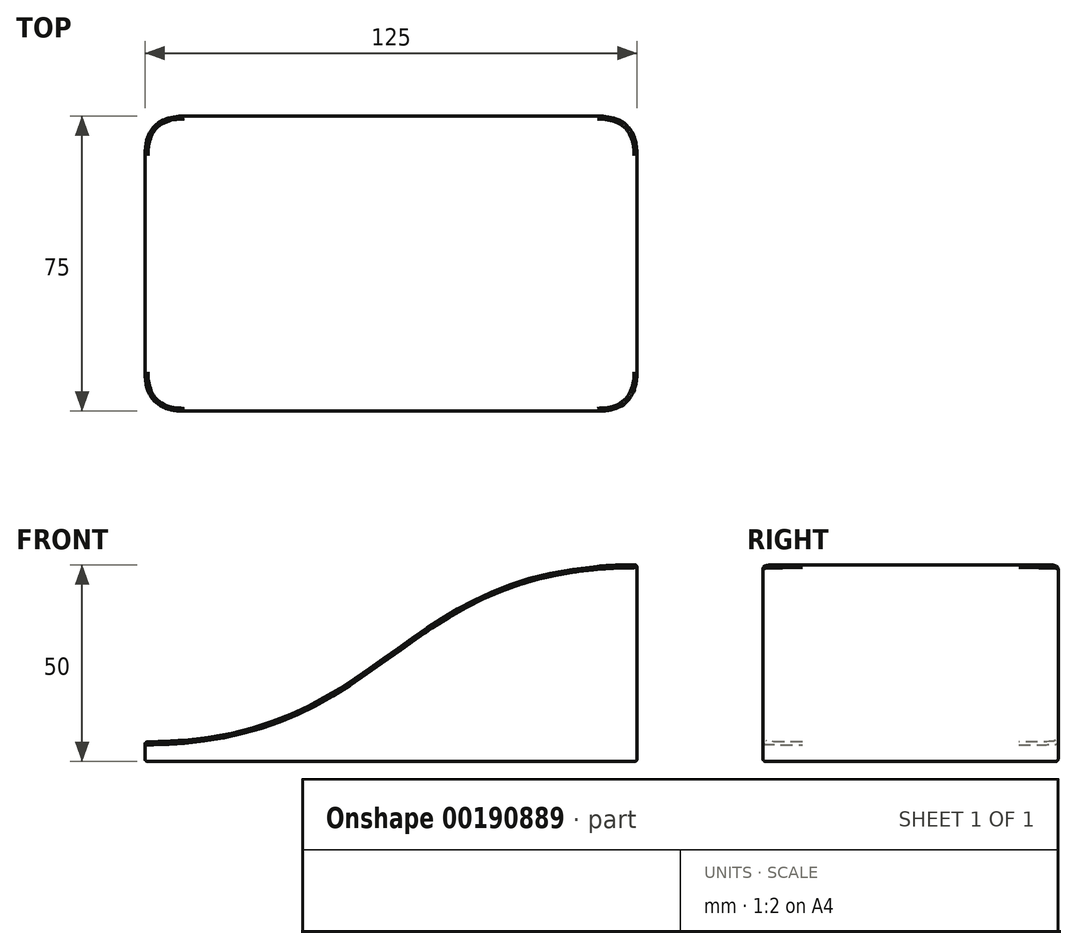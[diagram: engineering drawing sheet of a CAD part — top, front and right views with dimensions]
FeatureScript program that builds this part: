
annotation { "Feature Type Name" : "Feature", "Feature Type Description" : "" }
export const myFeature = defineFeature(function(context is Context, id is Id, definition is map)
    precondition{}
    {
        {
            var Q0;
            Q0=qCreatedBy(makeId("Front.planeOp"),FACE);
            var sketch = newSketch(context, id + "F0", { "sketchPlane" : qUnion([Q0])});
            skLineSegment(sketch, "E0", {"start": v(-62.5, 0) * mm, "end": v(62.5, 0) * mm});
            skLineSegment(sketch, "E1", {"start": v(-62.5, 0) * mm, "end": v(-62.5, 5) * mm});
            skLineSegment(sketch, "E2", {"start": v(62.5, 0) * mm, "end": v(62.5, 50) * mm});
            skFitSpline(sketch, "E3", {"points": [v(-62.5, 5) * mm, v(62.5, 50) * mm], "startDerivative": vector(187.5, 0) * mm, "endDerivative": vector(187.5, 0) * mm});
            skSolve(sketch);
        }
        {
            var Q0;
            Q0 = qSketchRegion(id + "F0", true);
            extrude(context, id + "F1", {"entities" : qUnion([Q0]), "depth" : 75 * mm, "symmetric" : true});
        }
        {
            var Q0;
            Q0=makeQuery(id+"F1.opExtrude","CAP_EDGE",EDGE,{"disambiguationData":[OSD([sQuery(id+"F0.wireOp",EDGE,"E1")])],"isStart":true});
            var Q1;
            Q1=makeQuery(id+"F1.opExtrude","CAP_EDGE",EDGE,{"disambiguationData":[OSD([sQuery(id+"F0.wireOp",EDGE,"E1")])],"isStart":false});
            var Q2;
            Q2=makeQuery(id+"F1.opExtrude","CAP_EDGE",EDGE,{"disambiguationData":[OSD([sQuery(id+"F0.wireOp",EDGE,"E2")])],"isStart":false});
            var Q3;
            Q3=makeQuery(id+"F1.opExtrude","CAP_EDGE",EDGE,{"disambiguationData":[OSD([sQuery(id+"F0.wireOp",EDGE,"E2")])],"isStart":true});
            fillet(context, id + "F2", {"entities" : qUnion([Q0, Q1, Q2, Q3]), "radius" : 10 * mm, "tangentPropagation" : true, "rho" : 0.5, "crossSection" : FilletCrossSection.CONIC, "allowEdgeOverflow" : false});
        }
        {
            var Q0;
            Q0=makeQuery(id+"F1.opExtrude","SWEPT_FACE",FACE,{"disambiguationData":[OSD([sQuery(id+"F0.wireOp",EDGE,"E3")])]});
            var Q1;
            Q1=makeQuery(id+"F1.opExtrude","SWEPT_FACE",FACE,{"disambiguationData":[OSD([sQuery(id+"F0.wireOp",EDGE,"E0")])]});
            fillet(context, id + "F3", {"entities" : qUnion([Q0, Q1]), "radius" : 0.75 * mm, "tangentPropagation" : true, "rho" : 0.5, "crossSection" : FilletCrossSection.CONIC, "allowEdgeOverflow" : false});
        }
    });
